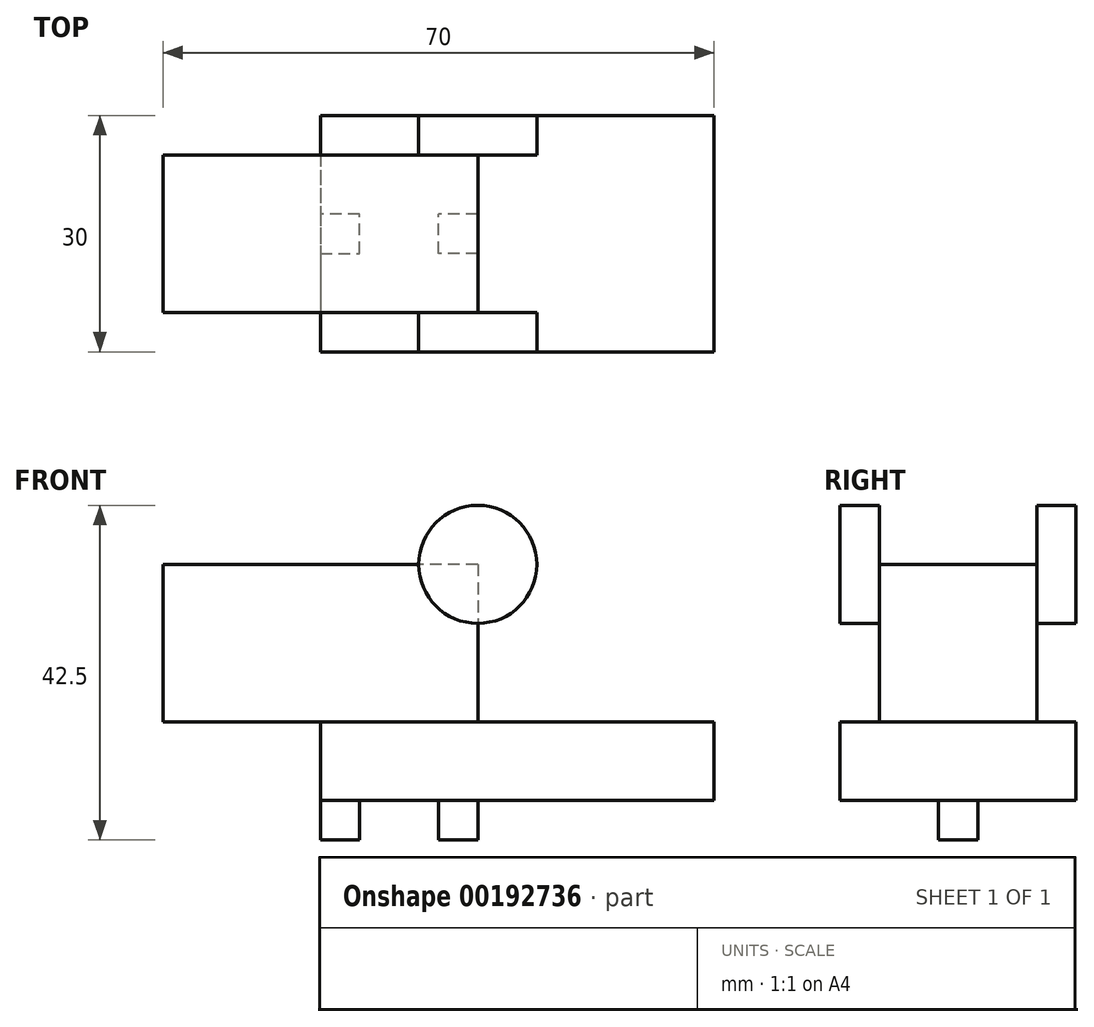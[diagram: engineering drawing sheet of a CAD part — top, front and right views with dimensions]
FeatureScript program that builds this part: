
annotation { "Feature Type Name" : "Feature", "Feature Type Description" : "" }
export const myFeature = defineFeature(function(context is Context, id is Id, definition is map)
    precondition{}
    {
        {
            var Q0;
            Q0=qCreatedBy(makeId("Top.planeOp"),FACE);
            var sketch = newSketch(context, id + "F0", { "sketchPlane" : qUnion([Q0])});
            skLineSegment(sketch, "E0.bottom", {"start": v(25, 15) * mm, "end": v(-25, 15) * mm});
            skLineSegment(sketch, "E0.top", {"start": v(25, -15) * mm, "end": v(-25, -15) * mm});
            skLineSegment(sketch, "E0.left", {"start": v(25, 15) * mm, "end": v(25, -15) * mm});
            skLineSegment(sketch, "E0.right", {"start": v(-25, 15) * mm, "end": v(-25, -15) * mm});
            skPoint(sketch, "E0.middle", {"position": v(0, 0) * mm});
            skSolve(sketch);
        }
        {
            var Q0;
            Q0 = qSketchRegion(id + "F0", true);
            extrude(context, id + "F1", {"entities" : qUnion([Q0]), "depth" : 10 * mm});
        }
        {
            var Q0;
            Q0=makeQuery(id+"F1.opExtrude","CAP_FACE",FACE,{"disambiguationData":[OSD([sQuery(id+"F0.wireOp",EDGE,"E0.bottom"),sQuery(id+"F0.wireOp",EDGE,"E0.top"),sQuery(id+"F0.wireOp",EDGE,"E0.left"),sQuery(id+"F0.wireOp",EDGE,"E0.right")])],"isStart":true});
            var sketch = newSketch(context, id + "F2", { "sketchPlane" : qUnion([Q0])});
            skLineSegment(sketch, "E1", {"start": v(-25, 0) * mm, "end": v(-25, 2.5) * mm});
            skLineSegment(sketch, "E2", {"start": v(-25, 2.5) * mm, "end": v(-20, 2.5) * mm});
            skLineSegment(sketch, "E3", {"start": v(-20, 2.5) * mm, "end": v(-20, -2.5) * mm});
            skLineSegment(sketch, "E4", {"start": v(-20, -2.5) * mm, "end": v(-25, -2.5) * mm});
            skLineSegment(sketch, "E5", {"start": v(-25, -2.5) * mm, "end": v(-25, 0) * mm});
            skLineSegment(sketch, "E6.bottom", {"start": v(-5, 2.5) * mm, "end": v(-10, 2.5) * mm});
            skLineSegment(sketch, "E6.top", {"start": v(-5, -2.5) * mm, "end": v(-10, -2.5) * mm});
            skLineSegment(sketch, "E6.left", {"start": v(-5, 2.5) * mm, "end": v(-5, -2.5) * mm});
            skLineSegment(sketch, "E6.right", {"start": v(-10, 2.5) * mm, "end": v(-10, -2.5) * mm});
            skPoint(sketch, "E6.middle", {"position": v(-7.5, 0) * mm});
            skLineSegment(sketch, "E7", {"start": v(-25, 0) * mm, "end": v(-22.5, 0) * mm, "construction": true});
            skSolve(sketch);
        }
        {
            var Q0;
            Q0 = qSketchRegion(id + "F2", true);
            extrude(context, id + "F3", {"entities" : qUnion([Q0]), "operationType" : NewBodyOperationType.ADD, "depth" : 5 * mm});
        }
        {
            var Q0;
            Q0=makeQuery(id+"F1.opExtrude","CAP_FACE",FACE,{"disambiguationData":[OSD([sQuery(id+"F0.wireOp",EDGE,"E0.bottom"),sQuery(id+"F0.wireOp",EDGE,"E0.top"),sQuery(id+"F0.wireOp",EDGE,"E0.left"),sQuery(id+"F0.wireOp",EDGE,"E0.right")])],"isStart":false});
            var sketch = newSketch(context, id + "F4", { "sketchPlane" : qUnion([Q0])});
            skLineSegment(sketch, "E8", {"start": v(-25, 10) * mm, "end": v(-5, 10) * mm});
            skLineSegment(sketch, "E9", {"start": v(-5, 10) * mm, "end": v(-5, -10) * mm});
            skLineSegment(sketch, "E10", {"start": v(-5, -10) * mm, "end": v(-25, -10) * mm});
            skLineSegment(sketch, "E11", {"start": v(-25, -10) * mm, "end": v(-25, 0) * mm});
            skLineSegment(sketch, "E12", {"start": v(-25, 0) * mm, "end": v(-25, 10) * mm});
            skSolve(sketch);
        }
        {
            var Q0;
            Q0 = qSketchRegion(id + "F4", true);
            extrude(context, id + "F5", {"entities" : qUnion([Q0]), "operationType" : NewBodyOperationType.ADD, "depth" : 20 * mm});
        }
        {
            var Q0;
            Q0=makeQuery(id+"F5.boolean.opBoolean","MERGE",FACE,{"derivedFrom":[makeQuery(id+"F3.boolean.opBoolean","MERGE",FACE,{"derivedFrom":[makeQuery(id+"F1.opExtrude","SWEPT_FACE",FACE,{"disambiguationData":[OSD([sQuery(id+"F0.wireOp",EDGE,"E0.right")])]}),makeQuery(id+"F3.opExtrude","SWEPT_FACE",FACE,{"disambiguationData":[OSD([sQuery(id+"F2.wireOp",EDGE,"E1"),sQuery(id+"F2.wireOp",EDGE,"E5")])]})]}),makeQuery(id+"F5.opExtrude","SWEPT_FACE",FACE,{"disambiguationData":[OSD([sQuery(id+"F4.wireOp",EDGE,"E11"),sQuery(id+"F4.wireOp",EDGE,"E12")])]})]});
            var sketch = newSketch(context, id + "F6", { "sketchPlane" : qUnion([Q0])});
            skPoint(sketch, "E13.endSnap0", {"position": v(0, 30) * mm});
            skLineSegment(sketch, "E14.bottom", {"start": v(-10, 30) * mm, "end": v(10, 30) * mm});
            skLineSegment(sketch, "E14.top", {"start": v(-10, 10) * mm, "end": v(10, 10) * mm});
            skLineSegment(sketch, "E14.left", {"start": v(-10, 30) * mm, "end": v(-10, 10) * mm});
            skLineSegment(sketch, "E14.right", {"start": v(10, 30) * mm, "end": v(10, 10) * mm});
            skSolve(sketch);
        }
        {
            var Q0;
            Q0 = qSketchRegion(id + "F6", true);
            extrude(context, id + "F7", {"entities" : qUnion([Q0]), "operationType" : NewBodyOperationType.ADD, "depth" : 20 * mm});
        }
        {
            var Q0;
            Q0=makeQuery(id+"F7.boolean.opBoolean","MERGE",FACE,{"derivedFrom":[makeQuery(id+"F5.opExtrude","SWEPT_FACE",FACE,{"disambiguationData":[OSD([sQuery(id+"F4.wireOp",EDGE,"E10")])]}),makeQuery(id+"F7.opExtrude","SWEPT_FACE",FACE,{"disambiguationData":[OSD([sQuery(id+"F6.wireOp",EDGE,"E14.right")])]})]});
            var sketch = newSketch(context, id + "F8", { "sketchPlane" : qUnion([Q0])});
            skCircle(sketch, "E15", {"center": v(-5, 30) * mm, "radius": 7.5 * mm});
            skSolve(sketch);
        }
        {
            var Q0;
            Q0 = qSketchRegion(id + "F8", true);
            extrude(context, id + "F9", {"entities" : qUnion([Q0]), "operationType" : NewBodyOperationType.ADD, "depth" : 5 * mm});
        }
        {
            var Q0;
            Q0=makeQuery(id+"F7.boolean.opBoolean","MERGE",FACE,{"derivedFrom":[makeQuery(id+"F5.opExtrude","SWEPT_FACE",FACE,{"disambiguationData":[OSD([sQuery(id+"F4.wireOp",EDGE,"E8")])]}),makeQuery(id+"F7.opExtrude","SWEPT_FACE",FACE,{"disambiguationData":[OSD([sQuery(id+"F6.wireOp",EDGE,"E14.left")])]})]});
            var sketch = newSketch(context, id + "F10", { "sketchPlane" : qUnion([Q0])});
            skCircle(sketch, "E16", {"center": v(5, 30) * mm, "radius": 7.5 * mm});
            skSolve(sketch);
        }
        {
            var Q0;
            Q0 = qSketchRegion(id + "F10", true);
            extrude(context, id + "F11", {"entities" : qUnion([Q0]), "operationType" : NewBodyOperationType.ADD, "depth" : 5 * mm});
        }
    });
